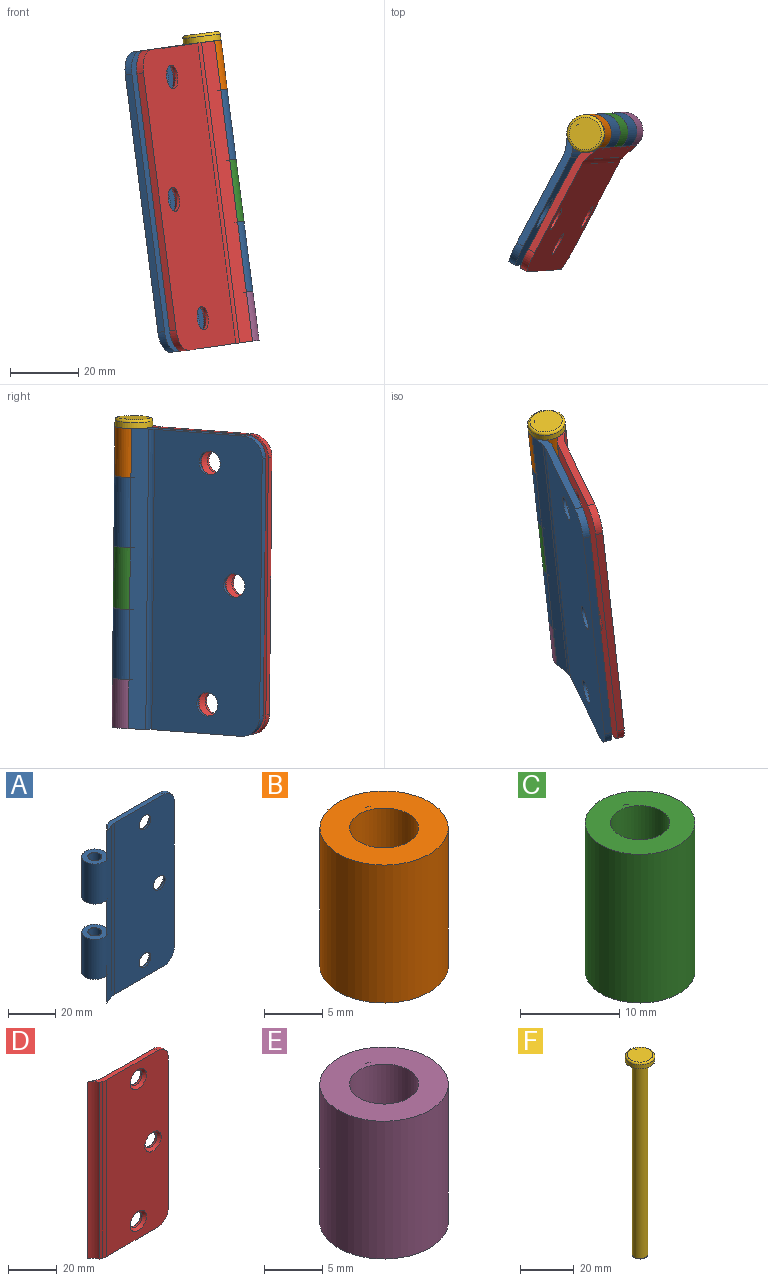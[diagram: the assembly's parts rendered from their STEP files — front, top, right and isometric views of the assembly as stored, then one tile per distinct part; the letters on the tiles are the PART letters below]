
ASSEMBLY  parts=6 mates=8
PART A: 32 faces, bbox 50x11.1x88.9 mm
  f0: cylinder r=5.53mm len=18.31mm, axis (0,0,1), area 90.4mm2, adj f2,f3,f16,f22
  f1: cylinder r=5.53mm len=14.55mm, axis (0,0,1), area 71.9mm2, adj f2,f3,f7,f17
  f2: plane 88.9x1.48mm, normal (-0.36,0.93,0), area 140.7mm2, adj f0,f1,f7,f8,f11,f15,f19,f31
  f3: plane 88.9x4.76mm, normal (0.36,-0.93,0), area 453.2mm2, adj f0,f1,f7,f8,f11,f15,f19,f30
  f4: plane 88.9x35.89mm, normal (0,-1,0), area 3057.4mm2, adj f5,f7,f8,f9,f10,f24,f25,f26
  f5: plane 76.2x2.21mm, normal (1,0,0), area 168.4mm2, adj f4,f6,f9,f10
  f6: plane 88.9x35.89mm, normal (0,1,0), area 2958.3mm2, adj f5,f7,f8,f9,f10,f27,f28,f29
  f7: plane 36.12x4.37mm, normal (0,0,1), area 74.4mm2, adj f1,f2,f3,f4,f6,f10,f30,f31
  f8: plane 36.12x4.37mm, normal (0,0,-1), area 74.4mm2, adj f2,f3,f4,f6,f9,f11,f30,f31
  f9: cylinder r=6.35mm len=6.35mm, axis (0,1,0), area 22mm2, adj f4,f5,f6,f8
  f10: cylinder r=6.35mm len=6.35mm, axis (0,-1,0), area 22mm2, adj f4,f5,f6,f7
  f11: cylinder r=5.53mm len=14.5mm, axis (0,0,1), area 71.6mm2, adj f2,f3,f8,f23
  f12: cylinder r=3.47mm len=20.75mm, axis (0,0,1), area 9.5mm2, adj f14,f16,f17
  f13: cylinder r=2.97mm len=20.75mm, axis (0,0,1), area 387.5mm2, adj f16,f17
  f14: plane 20.75x0.43mm, normal (0.36,0.93,0), area 9.5mm2, adj f12,f16,f17
  f15: cylinder r=5.53mm len=20.75mm, axis (0,0,1), area 618.4mm2, adj f2,f3,f16,f17
  f16: plane 11.06x11.06mm, normal (0,0,-1), area 68.3mm2, adj f0,f12,f13,f14,f15
  f17: plane 11.06x11.06mm, normal (0,0,1), area 68.3mm2, adj f1,f12,f13,f14,f15
  f18: plane 20.78x0.43mm, normal (0.36,0.93,0), area 9.5mm2, adj f20,f22,f23
  f19: cylinder r=5.53mm len=20.78mm, axis (0,0,-1), area 619.2mm2, adj f2,f3,f22,f23
  f20: cylinder r=3.47mm len=20.78mm, axis (0,0,-1), area 9.5mm2, adj f18,f22,f23
  f21: cylinder r=2.97mm len=20.78mm, axis (0,0,-1), area 388mm2, adj f22,f23
  f22: plane 11.06x11.06mm, normal (0,0,1), area 68.3mm2, adj f0,f18,f19,f20,f21
  f23: plane 11.06x11.06mm, normal (0,0,-1), area 68.3mm2, adj f11,f18,f19,f20,f21
  f24: cylinder r=3.51mm len=7.01mm, axis (0,1,0), area 20.7mm2, adj f4,f28
  f25: cylinder r=3.51mm len=7.01mm, axis (0,1,0), area 20.7mm2, adj f4,f29
  f26: cylinder r=3.51mm len=7.01mm, axis (0,1,0), area 20.7mm2, adj f4,f27
  f27: cone r=3.51mm half-angle=45deg, axis (0,1,0), area 46.7mm2, adj f6,f26
  f28: cone r=3.51mm half-angle=45deg, axis (0,1,0), area 46.7mm2, adj f6,f24
  f29: cone r=3.51mm half-angle=45deg, axis (0,1,0), area 46.7mm2, adj f6,f25
  f30: cylinder r=5.08mm len=88.9mm, axis (0,0,1), area 165.5mm2, adj f3,f4,f7,f8
  f31: cylinder r=5.08mm len=88.9mm, axis (0,0,1), area 165.5mm2, adj f2,f6,f7,f8
PART B: 6 faces, bbox 11.1x11.1x14.6 mm
  f0: cylinder r=3.47mm len=14.55mm, axis (0,0,1), area 6.7mm2, adj f1,f4,f5
  f1: plane 14.55x0.43mm, normal (0.36,0.93,0), area 6.7mm2, adj f0,f4,f5
  f2: cylinder r=2.97mm len=14.55mm, axis (0,0,1), area 271.8mm2, adj f4,f5
  f3: cylinder r=5.53mm len=14.55mm, axis (0,0,1), area 505.6mm2, adj f4,f5
  f4: plane 11.06x11.06mm, normal (0,0,-1), area 68.3mm2, adj f0,f1,f2,f3
  f5: plane 11.06x11.06mm, normal (0,0,1), area 68.3mm2, adj f0,f1,f2,f3
PART C: 6 faces, bbox 11.1x11.1x18.3 mm
  f0: cylinder r=3.47mm len=18.31mm, axis (0,0,1), area 8.4mm2, adj f1,f4,f5
  f1: plane 18.31x0.43mm, normal (0.36,0.93,0), area 8.4mm2, adj f0,f4,f5
  f2: cylinder r=2.97mm len=18.31mm, axis (0,0,1), area 342mm2, adj f4,f5
  f3: cylinder r=5.53mm len=18.31mm, axis (0,0,1), area 636.2mm2, adj f4,f5
  f4: plane 11.06x11.06mm, normal (0,0,-1), area 68.3mm2, adj f0,f1,f2,f3
  f5: plane 11.06x11.06mm, normal (0,0,1), area 68.3mm2, adj f0,f1,f2,f3
PART D: 18 faces, bbox 42.5x4.4x88.9 mm
  f0: plane 88.9x4.76mm, normal (0.36,0.93,0), area 453.3mm2, adj f5,f6,f7,f17
  f1: plane 88.9x1.48mm, normal (-0.36,-0.93,0), area 140.7mm2, adj f5,f6,f7,f16
  f2: plane 88.9x35.89mm, normal (0,-1,0), area 2958.5mm2, adj f3,f5,f6,f8,f9,f13,f14,f15
  f3: plane 76.2x2.22mm, normal (1,0,0), area 168.9mm2, adj f2,f4,f8,f9
  f4: plane 88.9x35.89mm, normal (0,1,0), area 3057.6mm2, adj f3,f5,f6,f8,f9,f10,f11,f12
  f5: plane 36.12x4.37mm, normal (0,0,1), area 74.7mm2, adj f0,f1,f2,f4,f7,f9,f16,f17
  f6: plane 36.12x4.37mm, normal (0,0,-1), area 74.7mm2, adj f0,f1,f2,f4,f7,f8,f16,f17
  f7: cylinder r=5.53mm len=88.9mm, axis (0,0,1), area 439.4mm2, adj f0,f1,f5,f6
  f8: cylinder r=6.35mm len=6.35mm, axis (0,1,0), area 22.1mm2, adj f2,f3,f4,f6
  f9: cylinder r=6.35mm len=6.35mm, axis (0,-1,0), area 22.1mm2, adj f2,f3,f4,f5
  f10: cylinder r=3.51mm len=7.01mm, axis (0,-1,0), area 20.9mm2, adj f4,f15
  f11: cylinder r=3.51mm len=7.01mm, axis (0,-1,0), area 20.9mm2, adj f4,f13
  f12: cylinder r=3.51mm len=7.01mm, axis (0,-1,0), area 20.9mm2, adj f4,f14
  f13: cone r=3.51mm half-angle=45deg, axis (0,-1,0), area 46.7mm2, adj f2,f11
  f14: cone r=3.51mm half-angle=45deg, axis (0,-1,0), area 46.7mm2, adj f2,f12
  f15: cone r=3.51mm half-angle=45deg, axis (0,-1,0), area 46.7mm2, adj f2,f10
  f16: cylinder r=5.08mm len=88.9mm, axis (0,0,-1), area 165mm2, adj f1,f2,f5,f6
  f17: cylinder r=5.08mm len=88.9mm, axis (0,0,-1), area 165mm2, adj f0,f4,f5,f6
PART E: 6 faces, bbox 11.1x11.1x14.5 mm
  f0: plane 14.5x0.43mm, normal (0.36,0.93,0), area 6.6mm2, adj f2,f4,f5
  f1: cylinder r=5.53mm len=14.5mm, axis (0,0,1), area 503.8mm2, adj f4,f5
  f2: cylinder r=3.47mm len=14.5mm, axis (0,0,1), area 6.6mm2, adj f0,f4,f5
  f3: cylinder r=2.97mm len=14.5mm, axis (0,0,1), area 270.8mm2, adj f4,f5
  f4: plane 11.06x11.06mm, normal (0,0,-1), area 68.3mm2, adj f0,f1,f2,f3
  f5: plane 11.06x11.06mm, normal (0,0,1), area 68.3mm2, adj f0,f1,f2,f3
PART F: 9 faces, bbox 12x12x91.4 mm
  f0: cylinder r=3.47mm len=2.54mm, axis (0,0,-1), area 1.2mm2, adj f1,f3,f4
  f1: plane 2.54x0.43mm, normal (0.36,0.93,0), area 1.2mm2, adj f0,f3,f4
  f2: cylinder r=5.53mm len=11.06mm, axis (0,0,-1), area 61.8mm2, adj f4,f5
  f3: plane 9.53x9.53mm, normal (0,0,1), area 71.4mm2, adj f0,f1,f5
  f4: plane 11.06x11.06mm, normal (0,0,-1), area 68.3mm2, adj f0,f1,f2,f6
  f5: torus R=4.77mm, axis (0,0,1), area 39.5mm2, adj f2,f3
  f6: cylinder r=2.97mm len=88.65mm, axis (0,0,1), area 1655.2mm2, adj f4,f8
  f7: plane 5.44x5.44mm, normal (0,0,-1), area 23.2mm2, adj f8
  f8: cone r=2.97mm half-angle=45deg, axis (0,0,1), area 6.4mm2, adj f6,f7
PLACE A rot(axis=(0.07,-0.03,-1),118.3deg) t=(130.85,117.2,-126.74)mm
PLACE B rot(axis=(0.07,-0.03,-1),118.2deg) t=(130.83,117.32,-126.74)mm
PLACE C rot(axis=(0.07,-0.03,-1),118.2deg) t=(130.83,117.32,-126.73)mm
PLACE D rot(axis=(0.07,-0.03,-1),118.2deg) t=(130.83,117.32,-126.74)mm
PLACE E rot(axis=(0.07,-0.03,-1),118.2deg) t=(130.83,117.32,-126.74)mm
PLACE F rot(axis=(-0.05,-0.11,0.99),62.3deg) t=(-8.72,92.21,-144.67)mm
MATE pin_slot F.f0 <-> B.f0  axis (0.13,0.01,-0.99) through (49.88,103.92,-47.51)mm
MATE revolute A.f0 <-> B.f0  axis (-0.13,-0.01,0.99) through (51.71,104.06,-61.95)mm
MATE pin_slot B.f0 <-> F.f0  axis (-0.13,-0.01,0.99) through (49.88,103.92,-47.51)mm
MATE cylindrical F.f0 <-> B.f0  axis (-0.13,-0.01,0.99) through (49.88,103.92,-47.51)mm
MATE fastened B.f0 <-> D.f7  axis (-0.13,-0.01,0.99) through (49.88,103.92,-47.51)mm
MATE fastened D.f7 <-> C.f0  axis (-0.13,-0.01,0.99) through (55.47,104.34,-91.61)mm
MATE fastened E.f1 <-> D.f7  axis (0.13,0.01,-0.99) through (61.05,104.77,-135.7)mm
MATE slider F.f0 <-> C.f0  axis (-0.13,-0.01,0.99) through (55.45,104.34,-91.48)mm
